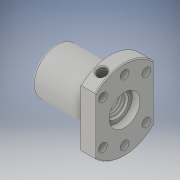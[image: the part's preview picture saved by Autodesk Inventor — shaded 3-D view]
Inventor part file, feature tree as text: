
AUTODESK INVENTOR PART (.ipt)
format: ipt  version: 2021 (Build 250183000, 183)  size: 236,544 bytes
history: native  units: mm
features: other x14, revolve x5, sketch x4, hole x2, thread x2, extrude x1, pattern_circular x1
ambient origin geometry x8: Origin, YZ Plane, XZ Plane, XY Plane, X Axis, Y Axis, Z Axis, Center Point
bodies: Solid1 (feature_tree)
feature tree (29):
  revolve  "Revolution1"  Angle=360.0deg
  revolve  "Revolution2"  Angle=45.0deg
  extrude  "Extrusion1"  Depth=7.4585mm TaperAngle=0.0deg
  hole  "Hole1"  [1 undecoded]
  pattern_circular  "Circular Pattern1"  Angle=360.0deg  [1 undecoded]
  revolve  "Revolution3"  [1 undecoded]
  thread  "Thread1"  [1 undecoded]
  revolve  "Revolution4"  [1 undecoded]
  hole  "Hole2"  [1 undecoded]
  revolve  "Revolution5"  [1 undecoded]
  thread  "Thread2"  [1 undecoded]
  other  "NUT_XY"
  other  "NUT_YZ"
  other  "NUT_ZX"
  other  "NUT_X"
  other  "NUT_Y"
  other  "NUT_Z"
  other  "NUT_Center"
  other  "NUT2_XY"
  other  "NUT2_YZ"
  other  "NUT2_ZX"
  other  "NUT2_X"
  other  "NUT2_Y"
  other  "NUT2_Z"
  other  "NUT2_Center"
  sketch  "Sketch_1"  dims[d0=360.0deg d1=360.0deg]
  sketch  "Sketch4"  dims[d2=8.0mm d3=0.0mm]
  sketch  "Sketch7"  dims[d4=4.5mm d5=6.0mm d6=4.0mm d7=2.0mm d8=90.0deg d9=8.0mm d10=0.0mm d11=80.0mm d12=45.0deg]
  sketch  "Sketch_8"  dims[d14=360.0deg d15=7.4585mm d16=0.0mm d17=360.0deg d18=16.0mm d19=6.0mm d20=4.0mm d21=2.0mm d22=90.0deg d23=4.0mm d24=0.0mm d25=360.0deg d26=26.376mm d27=0.0mm]
note: 8 required parameter values undecoded (feature->parameter linkage not recoverable at this tier; creation-order binding heuristic only, values carry confidence <= 0.55)